# Revit family: rechteck_211421_002_b147
name_source: partatom
category: Lighting Fixtures
units: mm (PartAtom-declared; Revit-internal decimal feet)

## family parameters
Cut with Voids When Loaded = No
Host = Face
Light Source = No
Part Type = Normal
Room Calculation Point = No
Round Connector Dimension = Use Diameter
Shared = No

## types (1)
- RECHTECK (1 x LED Modul 830, 850 lm, 3000)
    Apparent Load = 9 VA
    CIE Flux Codes = 33 61 84 71 100
    Color Rendering = 80
    Color Temperature = 3000
    Default Elevation = 1800 mm
    Description = Series: RECHTECK
Rectangular surface-mounted luminaire in classic design. Base: plastic. Opal glass: mouth-blown, satin finish. Diffuser fastening: spring system. Suitable for Ceiling mounting, Wall (surface). IP 43 ceiling mounting, IP 44 wall mounting. 
Colour: white
Length: 220 mm
Width: 120 mm
Height: 105 mm
Lamp: LED
Socket: without socket
Colour temperature: 3000K
Colour rendering index (CRI): 80
System power: 9 W
Rated luminous flux: 850 lm
Luminous efficiency: 94 lm/W
Control gear: Regulated power supply
Protection class: I
Type of protection: IP 43
    Height = 105 mm
    Lamp = 1 x LED Modul 830
    Lamp Light Flux = 850 lm
    Lamp count = 1
    Length = 220 mm
    Lifetime = 50000 h
    Luminous efficacy = 94 lm/W
    Manufacturer = RZB
    ModVariant = No
    Model = 211421.002
    Mounting Place = Ceiling, Wall
    Mounting Type = Surface mounted
    Number of Poles = 1
    OnlyDefault = Yes
    Power Factor = 1
    Product Name = RECHTECK
    Product group = Surface mounted ceiling and wall luminaires
    ProductGroupID = 305
    Protection Class = Protection class I
    Protection Degree = IP 43
    RLX_Detail_Level = 1
    RLX_Emergency_Light_Flux = 0 lm
    RLX_Emergency_Type = 0
    RLX_Emergency_Type_DB = No
    RlxData = <blob elided: 51321 chars, md5=2fc86116>
    Socket = socket
    Standby Power = 0 W
    System Light Flux = 850 lm
    System Power = 9 W
    Type Comments = Product without accessories
    Type Image = 21146.002.jpg
    URL = http://relux.com
    VarID = ---
    Voltage = 230 V
    Voltage Range = 220-240 V
    Weight = 0.00 kg
    Width = 120 mm

## geometry (parser evidence)
native form markers: Sweep x14
no freeform markers — native parametric forms only
